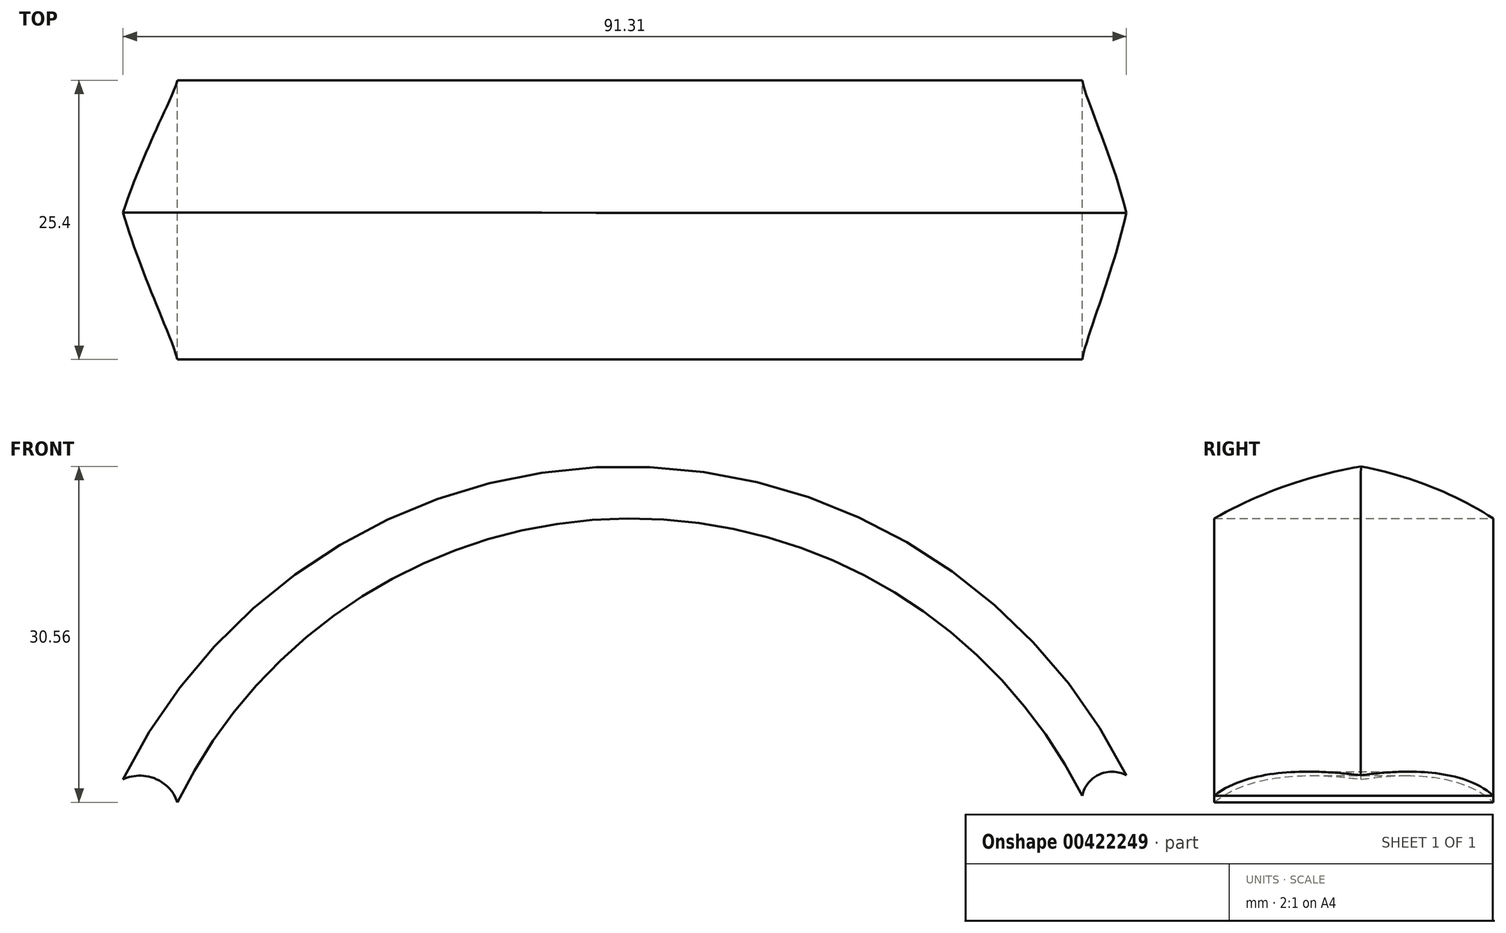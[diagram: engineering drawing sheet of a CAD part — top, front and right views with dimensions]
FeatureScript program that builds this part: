
annotation { "Feature Type Name" : "Feature", "Feature Type Description" : "" }
export const myFeature = defineFeature(function(context is Context, id is Id, definition is map)
    precondition{}
    {
        {
            var Q0;
            Q0=qCreatedBy(makeId("Front.planeOp"),FACE);
            var sketch = newSketch(context, id + "F0", { "sketchPlane" : qUnion([Q0])});
            skArc(sketch, "E0", {"start": v(44.4, 21.34) * mm, "mid": v(-2.83, 52.06) * mm, "end": v(-50.07, 21.34) * mm});
            skArc(sketch, "E1", {"start": v(38.94, 21.55) * mm, "mid": v(-2.41, 46.77) * mm, "end": v(-43.4, 20.94) * mm});
            skArc(sketch, "E2", {"start": v(-43.4, 20.94) * mm, "mid": v(-46.6, 23.36) * mm, "end": v(-50.07, 21.34) * mm});
            skArc(sketch, "E3", {"start": v(44.4, 21.34) * mm, "mid": v(41.76, 23.72) * mm, "end": v(38.94, 21.55) * mm});
            skSolve(sketch);
        }
        {
            var Q0;
            {var subQ4=sQuery(id+"F0.wireOp",EDGE,"E1");Q0=makeQuery(id+"F0.imprint","IMPRINT",FACE,{"disambiguationData":[TD([[makeQuery(id+"F0.imprint","IMPRINT",EDGE,{"derivedFrom":subQ4}),-1.0]])]});}
            extrude(context, id + "F1", {"entities" : qUnion([Q0]), "depth" : 25.4 * mm, "offsetDistance" : 25.4 * mm});
        }
        {
            var Q0;
            Q0=makeQuery(id+"F1.opExtrude","CAP_EDGE",EDGE,{"disambiguationData":[OSD([sQuery(id+"F0.wireOp",EDGE,"E0")])],"isStart":true});
            fillet(context, id + "F2", {"entities" : qUnion([Q0]), "radius" : 33.73 * mm, "tangentPropagation" : true, "allowEdgeOverflow" : false});
        }
        {
            var Q0;
            Q0=makeQuery(id+"F1.opExtrude","CAP_EDGE",EDGE,{"disambiguationData":[OSD([sQuery(id+"F0.wireOp",EDGE,"E0")])],"isStart":false});
            fillet(context, id + "F3", {"entities" : qUnion([Q0]), "radius" : 40.47 * mm, "tangentPropagation" : true, "allowEdgeOverflow" : false});
        }
    });
